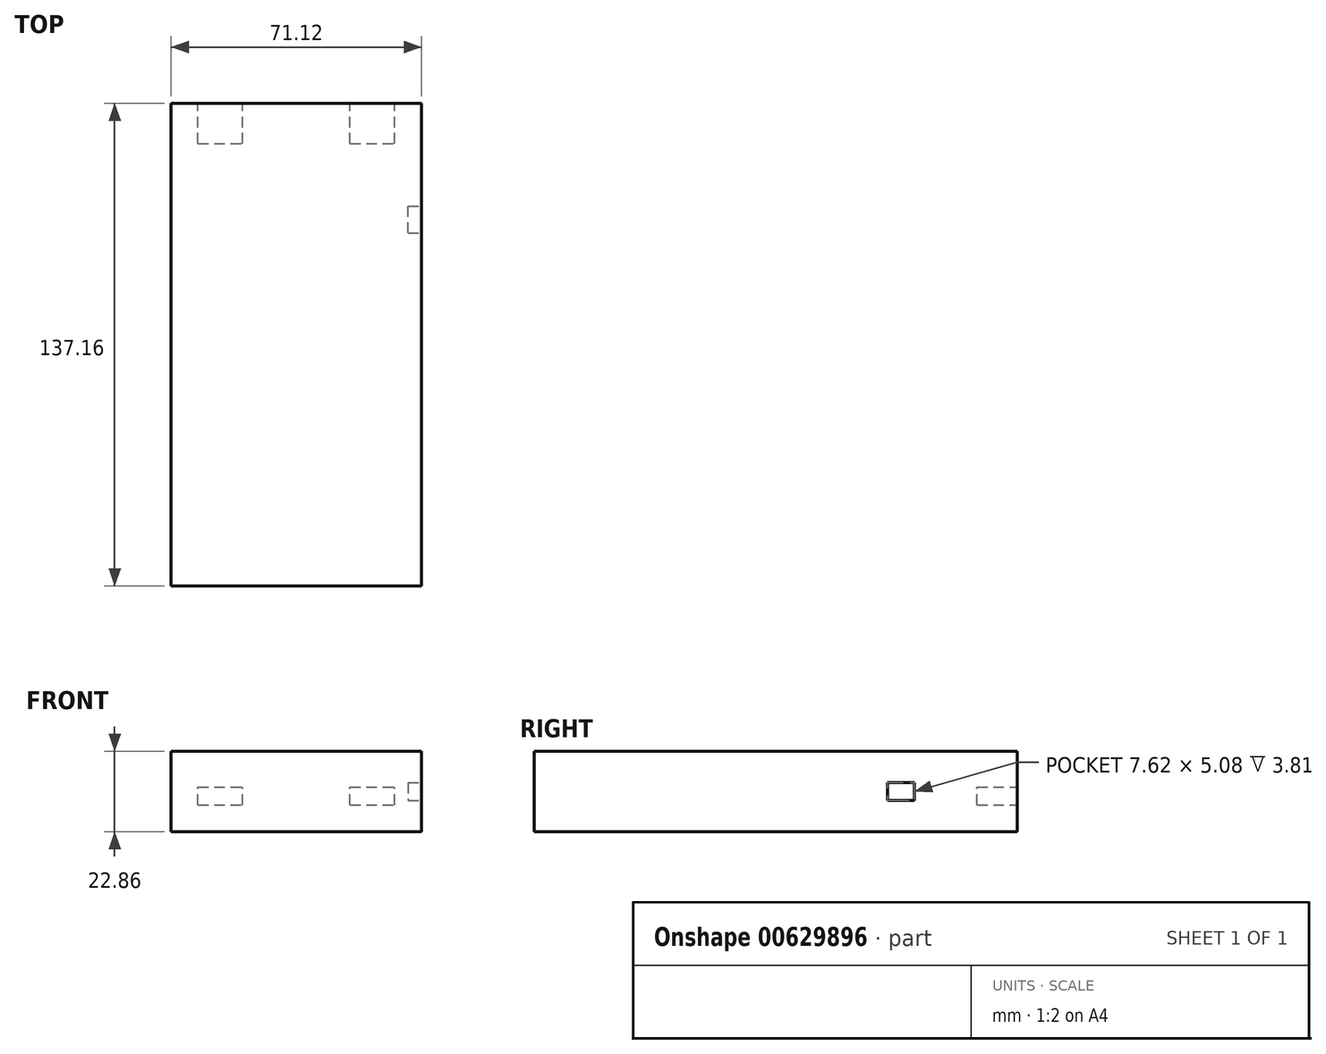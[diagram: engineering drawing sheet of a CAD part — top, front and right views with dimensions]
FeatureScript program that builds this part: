
annotation { "Feature Type Name" : "Feature", "Feature Type Description" : "" }
export const myFeature = defineFeature(function(context is Context, id is Id, definition is map)
    precondition{}
    {
        {
            var Q0;
            Q0=qCreatedBy(makeId("Top.planeOp"),FACE);
            var sketch = newSketch(context, id + "F0", { "sketchPlane" : qUnion([Q0])});
            skLineSegment(sketch, "E0.bottom", {"start": v(-51.34, 68.44) * mm, "end": v(19.78, 68.44) * mm});
            skLineSegment(sketch, "E0.top", {"start": v(-51.34, -68.72) * mm, "end": v(19.78, -68.72) * mm});
            skLineSegment(sketch, "E0.left", {"start": v(-51.34, 68.44) * mm, "end": v(-51.34, -68.72) * mm});
            skLineSegment(sketch, "E0.right", {"start": v(19.78, 68.44) * mm, "end": v(19.78, -68.72) * mm});
            skSolve(sketch);
        }
        {
            var Q0;
            Q0=makeQuery(id+"F0.imprint","IMPRINT",FACE,{"disambiguationData":[TD([[makeQuery(id+"F0.imprint","IMPRINT",EDGE,{"derivedFrom":sQuery(id+"F0.wireOp",EDGE,"E0.bottom")}),-1.0]])]});
            extrude(context, id + "F1", {"entities" : qUnion([Q0]), "depth" : 22.86 * mm, "offsetDistance" : 25.4 * mm});
        }
        {
            var Q0;
            Q0=makeQuery(id+"F1.opExtrude","SWEPT_FACE",FACE,{"disambiguationData":[OSD([sQuery(id+"F0.wireOp",EDGE,"E0.bottom")])]});
            var sketch = newSketch(context, id + "F2", { "sketchPlane" : qUnion([Q0])});
            skLineSegment(sketch, "E1.bottom", {"start": v(43.72, 7.62) * mm, "end": v(31.02, 7.62) * mm});
            skLineSegment(sketch, "E1.top", {"start": v(43.72, 12.7) * mm, "end": v(31.02, 12.7) * mm});
            skLineSegment(sketch, "E1.left", {"start": v(43.72, 7.62) * mm, "end": v(43.72, 12.7) * mm});
            skLineSegment(sketch, "E1.right", {"start": v(31.02, 7.62) * mm, "end": v(31.02, 12.7) * mm});
            skLineSegment(sketch, "E2.bottom", {"start": v(0.54, 7.62) * mm, "end": v(-12.16, 7.62) * mm});
            skLineSegment(sketch, "E2.top", {"start": v(0.54, 12.7) * mm, "end": v(-12.16, 12.7) * mm});
            skLineSegment(sketch, "E2.left", {"start": v(0.54, 7.62) * mm, "end": v(0.54, 12.7) * mm});
            skLineSegment(sketch, "E2.right", {"start": v(-12.16, 7.62) * mm, "end": v(-12.16, 12.7) * mm});
            skSolve(sketch);
        }
        {
            var Q0;
            Q0=makeQuery(id+"F2.imprint","IMPRINT",FACE,{"disambiguationData":[TD([[makeQuery(id+"F2.imprint","IMPRINT",EDGE,{"derivedFrom":sQuery(id+"F2.wireOp",EDGE,"E2.bottom")}),-1.0]])]});
            var Q1;
            Q1=makeQuery(id+"F2.imprint","IMPRINT",FACE,{"disambiguationData":[TD([[makeQuery(id+"F2.imprint","IMPRINT",EDGE,{"derivedFrom":sQuery(id+"F2.wireOp",EDGE,"E1.bottom")}),-1.0]])]});
            extrude(context, id + "F3", {"entities" : qUnion([Q0, Q1]), "operationType" : NewBodyOperationType.REMOVE, "oppositeDirection" : true, "depth" : 11.43 * mm, "offsetDistance" : 25.4 * mm});
        }
        {
            var Q0;
            Q0=makeQuery(id+"F1.opExtrude","SWEPT_FACE",FACE,{"disambiguationData":[OSD([sQuery(id+"F0.wireOp",EDGE,"E0.right")])]});
            var sketch = newSketch(context, id + "F4", { "sketchPlane" : qUnion([Q0])});
            skLineSegment(sketch, "E3.bottom", {"start": v(31.6, 13.97) * mm, "end": v(39.23, 13.97) * mm});
            skLineSegment(sketch, "E3.top", {"start": v(31.6, 8.9) * mm, "end": v(39.23, 8.9) * mm});
            skLineSegment(sketch, "E3.left", {"start": v(31.6, 13.97) * mm, "end": v(31.6, 8.9) * mm});
            skLineSegment(sketch, "E3.right", {"start": v(39.23, 13.97) * mm, "end": v(39.23, 8.9) * mm});
            skSolve(sketch);
        }
        {
            var Q0;
            Q0=makeQuery(id+"F4.imprint","IMPRINT",FACE,{"disambiguationData":[TD([[makeQuery(id+"F4.imprint","IMPRINT",EDGE,{"derivedFrom":sQuery(id+"F4.wireOp",EDGE,"E3.bottom")}),-1.0]])]});
            extrude(context, id + "F5", {"entities" : qUnion([Q0]), "operationType" : NewBodyOperationType.REMOVE, "oppositeDirection" : true, "depth" : 3.8 * mm, "offsetDistance" : 25.4 * mm});
        }
    });
